# Revit family: Toilet-Paper-Holder-American_Standard-Townsend-7455230_Series
name_source: partatom
category: Specialty Equipment
units: mm (PartAtom-declared; Revit-internal decimal feet)

## family parameters
Cut with Voids When Loaded = No
Host = Face
OmniClass Number = 23.40.20.21.21
OmniClass Title = Toilet Paper Dispensers
Part Type = Normal
Room Calculation Point = No
Round Connector Dimension = Use Diameter
Shared = Yes

## types (6) — shared parameters
Assembly Code = C1030220
Default Elevation = 48"
Description = Town Square® S Toilet Paper Holder
Finish = Metal-American Standard-002-Polished Chrome
Height = 2 1/4"
Installation Type = Wall Mount
Length = 8 29/32"
Manufacturer = American Standard
Material = Metal-American Standard-002-Polished Chrome
Product Documentation Link = https://lixil.cdn.celum.cloud
Product Page URL = https://www.americanstandard-us.com
Revised Date = 02/28/2024
URL = https://www.americanstandard-us.com
Warranty Information = Limited Lifetime Warranty
Width = 3 7/16"

## type names (no varying parameters)
- 7455230.013
- 7455230.278
- 7455230.002
- 7455230.243
- 7455230.GN0
- 7455230.295

note: column(s) folded — value = type name in every type: Model

## geometry (parser evidence)
native form markers: Sweep x2
no freeform markers — native parametric forms only
